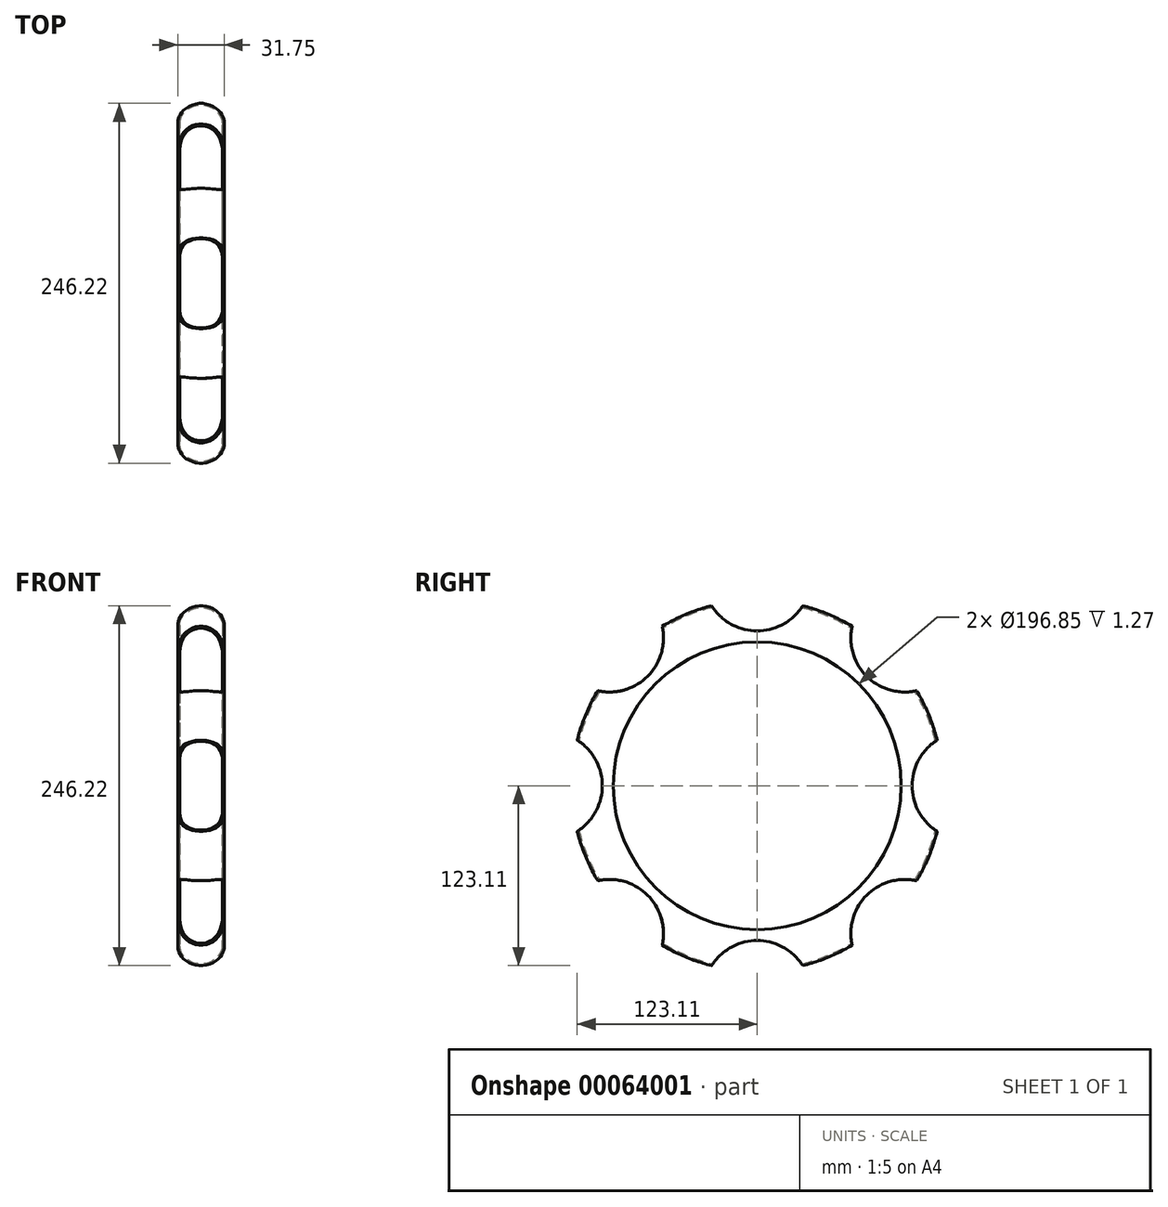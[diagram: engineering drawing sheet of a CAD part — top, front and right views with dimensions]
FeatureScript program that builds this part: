
annotation { "Feature Type Name" : "Feature", "Feature Type Description" : "" }
export const myFeature = defineFeature(function(context is Context, id is Id, definition is map)
    precondition{}
    {
        {
            var Q0;
            Q0=qCreatedBy(makeId("Front.planeOp"),FACE);
            var sketch = newSketch(context, id + "F0", { "sketchPlane" : qUnion([Q0])});
            skLineSegment(sketch, "E0", {"start": v(0, 98.43) * mm, "end": v(0, 111.12) * mm});
            skLineSegment(sketch, "E1", {"start": v(31.75, 111.12) * mm, "end": v(31.75, 98.43) * mm});
            skArc(sketch, "E2", {"start": v(31.75, 111.12) * mm, "mid": v(15.87, 127) * mm, "end": v(0, 111.12) * mm});
            skLineSegment(sketch, "E3", {"start": v(0, 0) * mm, "end": v(51.83, 0) * mm, "construction": true});
            skLineSegment(sketch, "E4", {"start": v(0, 98.43) * mm, "end": v(31.75, 98.43) * mm});
            skSolve(sketch);
        }
        {
            var Q0;
            Q0 = qSketchRegion(id + "F0", true);
            var Q1;
            Q1=sQuery(id+"F0.wireOp",EDGE,"E2");
            var Q2;
            Q2=sQuery(id+"F0.wireOp",EDGE,"E1");
            var Q3;
            Q3=sQuery(id+"F0.wireOp",EDGE,"E0");
            var Q4;
            Q4=sQuery(id+"F0.wireOp",EDGE,"E3");
            revolve(context, id + "F1", {"entities" : qUnion([Q0]), "surfaceEntities" : qUnion([Q1, Q2, Q3]), "axis" : qUnion([Q4]), "revolveType" : RevolveType.FULL});
        }
        {
            var Q0;
            Q0=makeQuery(id+"F1.opRevolve","SWEPT_FACE",FACE,{"disambiguationData":[OSD([sQuery(id+"F0.wireOp",EDGE,"E4")])]});
            shell(context, id + "F2", {"entities" : qUnion([Q0]), "thickness" : 1.27 * mm});
        }
        {
            var Q0;
            Q0=makeQuery(id+"F1.opRevolve","SWEPT_FACE",FACE,{"disambiguationData":[OSD([sQuery(id+"F0.wireOp",EDGE,"E1")])]});
            var sketch = newSketch(context, id + "F3", { "sketchPlane" : qUnion([Q0])});
            skCircle(sketch, "E5", {"center": v(0, 142.85) * mm, "radius": 36.9 * mm});
            skCircle(sketch, "E6.1.0", {"center": v(-101.01, 101.01) * mm, "radius": 36.9 * mm});
            skCircle(sketch, "E6.2.0", {"center": v(-142.85, 0) * mm, "radius": 36.9 * mm});
            skCircle(sketch, "E6.3.0", {"center": v(-101.01, -101.01) * mm, "radius": 36.9 * mm});
            skCircle(sketch, "E6.4.0", {"center": v(0, -142.85) * mm, "radius": 36.9 * mm});
            skCircle(sketch, "E6.5.0", {"center": v(101.01, -101.01) * mm, "radius": 36.9 * mm});
            skCircle(sketch, "E6.6.0", {"center": v(142.85, 0) * mm, "radius": 36.9 * mm});
            skCircle(sketch, "E6.7.0", {"center": v(101.01, 101.01) * mm, "radius": 36.9 * mm});
            skPoint(sketch, "E6.center", {"position": v(0, 0) * mm});
            skSolve(sketch);
        }
        {
            var Q0;
            {var subQ0=sQuery(id+"F3.wireOp",EDGE,"E5");var subQ1=makeQuery(id+"F1.opRevolve","SWEPT_EDGE",EDGE,{"disambiguationData":[OSD([sQuery(id+"F0.wireOp",EDGE,"E1"),sQuery(id+"F0.wireOp",EDGE,"E2")])]});var subQ2=makeQuery(id+"F3.imprint","INTERSECT",VERTEX,{"disambiguationData":[OD(0.0)],"derivedFrom":[subQ1,subQ0]});Q0=makeQuery(id+"F3.imprint","IMPRINT",FACE,{"disambiguationData":[TD([[makeQuery(id+"F3.imprint","IMPRINT",EDGE,{"disambiguationData":[TD([[subQ2,-1.0]])],"derivedFrom":subQ0}),1.0]])]});}
            var Q1;
            {var subQ0=sQuery(id+"F3.wireOp",EDGE,"E5");var subQ1=makeQuery(id+"F1.opRevolve","SWEPT_EDGE",EDGE,{"disambiguationData":[OSD([sQuery(id+"F0.wireOp",EDGE,"E1"),sQuery(id+"F0.wireOp",EDGE,"E2")])]});var subQ2=makeQuery(id+"F3.imprint","INTERSECT",VERTEX,{"disambiguationData":[OD(0.0)],"derivedFrom":[subQ1,subQ0]});Q1=makeQuery(id+"F3.imprint","IMPRINT",FACE,{"disambiguationData":[TD([[makeQuery(id+"F3.imprint","IMPRINT",EDGE,{"disambiguationData":[TD([[subQ2,1.0]])],"derivedFrom":subQ0}),1.0]])]});}
            var Q2;
            {var subQ0=sQuery(id+"F3.wireOp",EDGE,"E6.1.0");var subQ1=makeQuery(id+"F1.opRevolve","SWEPT_EDGE",EDGE,{"disambiguationData":[OSD([sQuery(id+"F0.wireOp",EDGE,"E1"),sQuery(id+"F0.wireOp",EDGE,"E2")])]});var subQ2=makeQuery(id+"F3.imprint","INTERSECT",VERTEX,{"disambiguationData":[OD(0.0)],"derivedFrom":[subQ1,subQ0]});Q2=makeQuery(id+"F3.imprint","IMPRINT",FACE,{"disambiguationData":[TD([[makeQuery(id+"F3.imprint","IMPRINT",EDGE,{"disambiguationData":[TD([[subQ2,-1.0]])],"derivedFrom":subQ0}),1.0]])]});}
            var Q3;
            {var subQ0=sQuery(id+"F3.wireOp",EDGE,"E6.1.0");var subQ1=makeQuery(id+"F1.opRevolve","SWEPT_EDGE",EDGE,{"disambiguationData":[OSD([sQuery(id+"F0.wireOp",EDGE,"E1"),sQuery(id+"F0.wireOp",EDGE,"E2")])]});var subQ2=makeQuery(id+"F3.imprint","INTERSECT",VERTEX,{"disambiguationData":[OD(0.0)],"derivedFrom":[subQ1,subQ0]});Q3=makeQuery(id+"F3.imprint","IMPRINT",FACE,{"disambiguationData":[TD([[makeQuery(id+"F3.imprint","IMPRINT",EDGE,{"disambiguationData":[TD([[subQ2,1.0]])],"derivedFrom":subQ0}),1.0]])]});}
            var Q4;
            {var subQ0=sQuery(id+"F3.wireOp",EDGE,"E6.2.0");var subQ1=makeQuery(id+"F1.opRevolve","SWEPT_EDGE",EDGE,{"disambiguationData":[OSD([sQuery(id+"F0.wireOp",EDGE,"E1"),sQuery(id+"F0.wireOp",EDGE,"E2")])]});var subQ2=makeQuery(id+"F3.imprint","INTERSECT",VERTEX,{"disambiguationData":[OD(0.0)],"derivedFrom":[subQ1,subQ0]});Q4=makeQuery(id+"F3.imprint","IMPRINT",FACE,{"disambiguationData":[TD([[makeQuery(id+"F3.imprint","IMPRINT",EDGE,{"disambiguationData":[TD([[subQ2,1.0]])],"derivedFrom":subQ0}),1.0]])]});}
            var Q5;
            {var subQ0=sQuery(id+"F3.wireOp",EDGE,"E6.2.0");var subQ1=makeQuery(id+"F1.opRevolve","SWEPT_EDGE",EDGE,{"disambiguationData":[OSD([sQuery(id+"F0.wireOp",EDGE,"E1"),sQuery(id+"F0.wireOp",EDGE,"E2")])]});var subQ2=makeQuery(id+"F3.imprint","INTERSECT",VERTEX,{"disambiguationData":[OD(0.0)],"derivedFrom":[subQ1,subQ0]});Q5=makeQuery(id+"F3.imprint","IMPRINT",FACE,{"disambiguationData":[TD([[makeQuery(id+"F3.imprint","IMPRINT",EDGE,{"disambiguationData":[TD([[subQ2,-1.0]])],"derivedFrom":subQ0}),1.0]])]});}
            var Q6;
            {var subQ0=sQuery(id+"F3.wireOp",EDGE,"E6.3.0");var subQ1=makeQuery(id+"F1.opRevolve","SWEPT_EDGE",EDGE,{"disambiguationData":[OSD([sQuery(id+"F0.wireOp",EDGE,"E1"),sQuery(id+"F0.wireOp",EDGE,"E2")])]});var subQ2=makeQuery(id+"F3.imprint","INTERSECT",VERTEX,{"disambiguationData":[OD(0.0)],"derivedFrom":[subQ1,subQ0]});Q6=makeQuery(id+"F3.imprint","IMPRINT",FACE,{"disambiguationData":[TD([[makeQuery(id+"F3.imprint","IMPRINT",EDGE,{"disambiguationData":[TD([[subQ2,-1.0]])],"derivedFrom":subQ0}),1.0]])]});}
            var Q7;
            {var subQ0=sQuery(id+"F3.wireOp",EDGE,"E6.3.0");var subQ1=makeQuery(id+"F1.opRevolve","SWEPT_EDGE",EDGE,{"disambiguationData":[OSD([sQuery(id+"F0.wireOp",EDGE,"E1"),sQuery(id+"F0.wireOp",EDGE,"E2")])]});var subQ2=makeQuery(id+"F3.imprint","INTERSECT",VERTEX,{"disambiguationData":[OD(0.0)],"derivedFrom":[subQ1,subQ0]});Q7=makeQuery(id+"F3.imprint","IMPRINT",FACE,{"disambiguationData":[TD([[makeQuery(id+"F3.imprint","IMPRINT",EDGE,{"disambiguationData":[TD([[subQ2,1.0]])],"derivedFrom":subQ0}),1.0]])]});}
            var Q8;
            {var subQ0=sQuery(id+"F3.wireOp",EDGE,"E6.4.0");var subQ1=makeQuery(id+"F1.opRevolve","SWEPT_EDGE",EDGE,{"disambiguationData":[OSD([sQuery(id+"F0.wireOp",EDGE,"E1"),sQuery(id+"F0.wireOp",EDGE,"E2")])]});var subQ2=makeQuery(id+"F3.imprint","INTERSECT",VERTEX,{"disambiguationData":[OD(0.0)],"derivedFrom":[subQ1,subQ0]});Q8=makeQuery(id+"F3.imprint","IMPRINT",FACE,{"disambiguationData":[TD([[makeQuery(id+"F3.imprint","IMPRINT",EDGE,{"disambiguationData":[TD([[subQ2,1.0]])],"derivedFrom":subQ0}),1.0]])]});}
            var Q9;
            {var subQ0=sQuery(id+"F3.wireOp",EDGE,"E6.4.0");var subQ1=makeQuery(id+"F1.opRevolve","SWEPT_EDGE",EDGE,{"disambiguationData":[OSD([sQuery(id+"F0.wireOp",EDGE,"E1"),sQuery(id+"F0.wireOp",EDGE,"E2")])]});var subQ2=makeQuery(id+"F3.imprint","INTERSECT",VERTEX,{"disambiguationData":[OD(0.0)],"derivedFrom":[subQ1,subQ0]});Q9=makeQuery(id+"F3.imprint","IMPRINT",FACE,{"disambiguationData":[TD([[makeQuery(id+"F3.imprint","IMPRINT",EDGE,{"disambiguationData":[TD([[subQ2,-1.0]])],"derivedFrom":subQ0}),1.0]])]});}
            var Q10;
            {var subQ0=sQuery(id+"F3.wireOp",EDGE,"E6.5.0");var subQ1=makeQuery(id+"F1.opRevolve","SWEPT_EDGE",EDGE,{"disambiguationData":[OSD([sQuery(id+"F0.wireOp",EDGE,"E1"),sQuery(id+"F0.wireOp",EDGE,"E2")])]});var subQ2=makeQuery(id+"F3.imprint","INTERSECT",VERTEX,{"disambiguationData":[OD(0.0)],"derivedFrom":[subQ1,subQ0]});Q10=makeQuery(id+"F3.imprint","IMPRINT",FACE,{"disambiguationData":[TD([[makeQuery(id+"F3.imprint","IMPRINT",EDGE,{"disambiguationData":[TD([[subQ2,-1.0]])],"derivedFrom":subQ0}),1.0]])]});}
            var Q11;
            {var subQ0=sQuery(id+"F3.wireOp",EDGE,"E6.5.0");var subQ1=makeQuery(id+"F1.opRevolve","SWEPT_EDGE",EDGE,{"disambiguationData":[OSD([sQuery(id+"F0.wireOp",EDGE,"E1"),sQuery(id+"F0.wireOp",EDGE,"E2")])]});var subQ2=makeQuery(id+"F3.imprint","INTERSECT",VERTEX,{"disambiguationData":[OD(0.0)],"derivedFrom":[subQ1,subQ0]});Q11=makeQuery(id+"F3.imprint","IMPRINT",FACE,{"disambiguationData":[TD([[makeQuery(id+"F3.imprint","IMPRINT",EDGE,{"disambiguationData":[TD([[subQ2,1.0]])],"derivedFrom":subQ0}),1.0]])]});}
            var Q12;
            {var subQ0=sQuery(id+"F3.wireOp",EDGE,"E6.6.0");var subQ1=makeQuery(id+"F1.opRevolve","SWEPT_EDGE",EDGE,{"disambiguationData":[OSD([sQuery(id+"F0.wireOp",EDGE,"E1"),sQuery(id+"F0.wireOp",EDGE,"E2")])]});var subQ2=makeQuery(id+"F3.imprint","INTERSECT",VERTEX,{"disambiguationData":[OD(0.0)],"derivedFrom":[subQ1,subQ0]});Q12=makeQuery(id+"F3.imprint","IMPRINT",FACE,{"disambiguationData":[TD([[makeQuery(id+"F3.imprint","IMPRINT",EDGE,{"disambiguationData":[TD([[subQ2,-1.0]])],"derivedFrom":subQ0}),1.0]])]});}
            var Q13;
            {var subQ0=sQuery(id+"F3.wireOp",EDGE,"E6.6.0");var subQ1=makeQuery(id+"F1.opRevolve","SWEPT_EDGE",EDGE,{"disambiguationData":[OSD([sQuery(id+"F0.wireOp",EDGE,"E1"),sQuery(id+"F0.wireOp",EDGE,"E2")])]});var subQ2=makeQuery(id+"F3.imprint","INTERSECT",VERTEX,{"disambiguationData":[OD(0.0)],"derivedFrom":[subQ1,subQ0]});Q13=makeQuery(id+"F3.imprint","IMPRINT",FACE,{"disambiguationData":[TD([[makeQuery(id+"F3.imprint","IMPRINT",EDGE,{"disambiguationData":[TD([[subQ2,1.0]])],"derivedFrom":subQ0}),1.0]])]});}
            var Q14;
            {var subQ0=sQuery(id+"F3.wireOp",EDGE,"E6.7.0");var subQ1=makeQuery(id+"F1.opRevolve","SWEPT_EDGE",EDGE,{"disambiguationData":[OSD([sQuery(id+"F0.wireOp",EDGE,"E1"),sQuery(id+"F0.wireOp",EDGE,"E2")])]});var subQ2=makeQuery(id+"F3.imprint","INTERSECT",VERTEX,{"disambiguationData":[OD(0.0)],"derivedFrom":[subQ1,subQ0]});Q14=makeQuery(id+"F3.imprint","IMPRINT",FACE,{"disambiguationData":[TD([[makeQuery(id+"F3.imprint","IMPRINT",EDGE,{"disambiguationData":[TD([[subQ2,1.0]])],"derivedFrom":subQ0}),1.0]])]});}
            var Q15;
            {var subQ0=sQuery(id+"F3.wireOp",EDGE,"E6.7.0");var subQ1=makeQuery(id+"F1.opRevolve","SWEPT_EDGE",EDGE,{"disambiguationData":[OSD([sQuery(id+"F0.wireOp",EDGE,"E1"),sQuery(id+"F0.wireOp",EDGE,"E2")])]});var subQ2=makeQuery(id+"F3.imprint","INTERSECT",VERTEX,{"disambiguationData":[OD(0.0)],"derivedFrom":[subQ1,subQ0]});Q15=makeQuery(id+"F3.imprint","IMPRINT",FACE,{"disambiguationData":[TD([[makeQuery(id+"F3.imprint","IMPRINT",EDGE,{"disambiguationData":[TD([[subQ2,-1.0]])],"derivedFrom":subQ0}),1.0]])]});}
            var Q16;
            Q16=sQuery(id+"F3.wireOp",EDGE,"E5");
            extrude(context, id + "F4", {"entities" : qUnion([Q0, Q1, Q2, Q3, Q4, Q5, Q6, Q7, Q8, Q9, Q10, Q11, Q12, Q13, Q14, Q15]), "operationType" : NewBodyOperationType.REMOVE, "surfaceEntities" : qUnion([Q16]), "endBound" : BoundingType.THROUGH_ALL, "oppositeDirection" : true, "depth" : 25.4 * mm});
        }
    });
